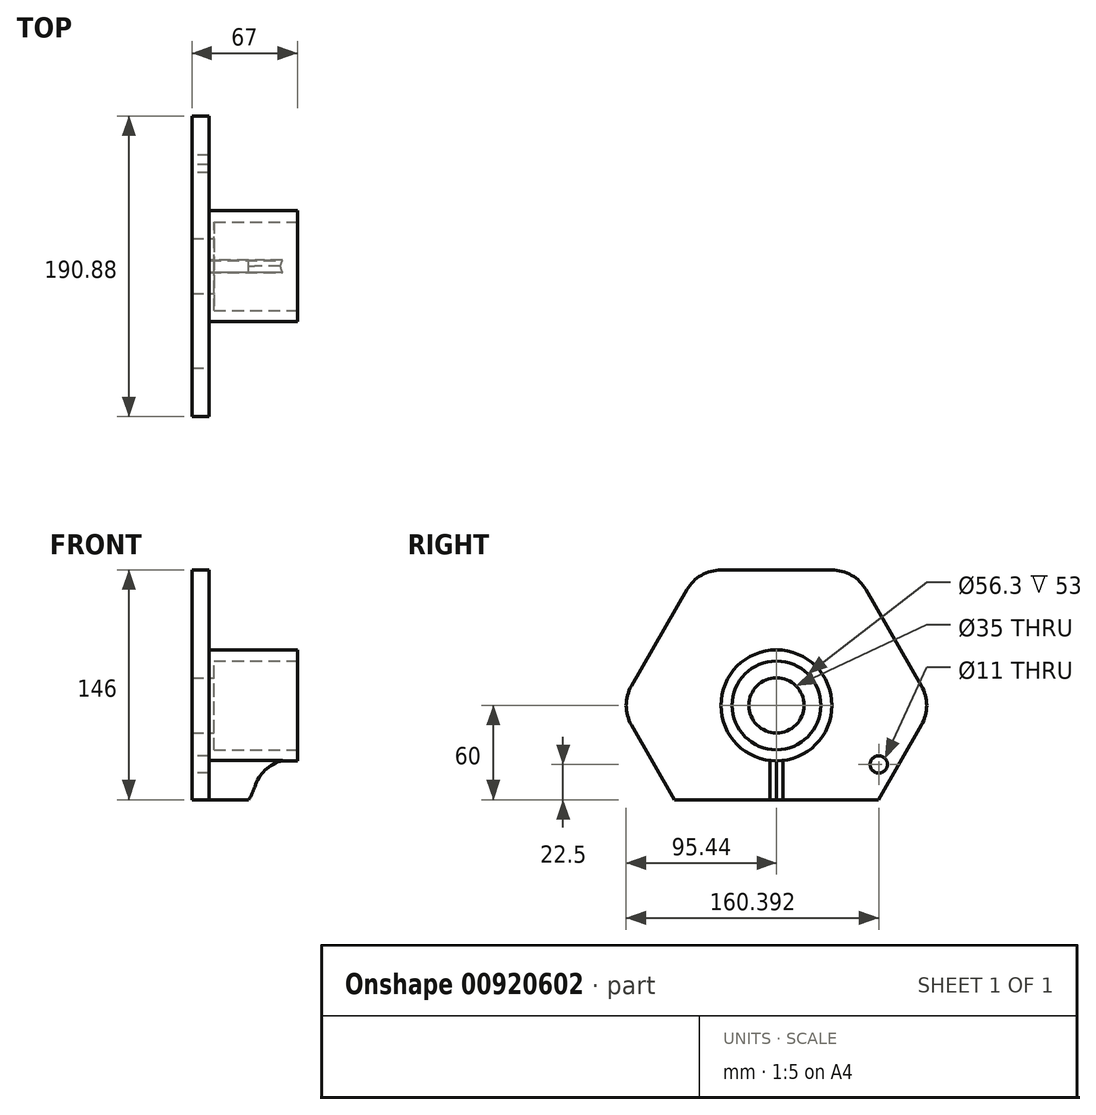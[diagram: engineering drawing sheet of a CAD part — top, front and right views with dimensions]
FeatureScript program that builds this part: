
annotation { "Feature Type Name" : "Feature", "Feature Type Description" : "" }
export const myFeature = defineFeature(function(context is Context, id is Id, definition is map)
    precondition{}
    {
        {
            var Q0;
            Q0=qCreatedBy(makeId("Front.planeOp"),FACE);
            var sketch = newSketch(context, id + "F0", { "sketchPlane" : qUnion([Q0])});
            skLineSegment(sketch, "E0.bottom", {"start": v(67, 35.25) * mm, "end": v(0, 35.25) * mm});
            skLineSegment(sketch, "E0.top", {"start": v(67, 28.15) * mm, "end": v(14, 28.15) * mm});
            skLineSegment(sketch, "E0.left", {"start": v(67, 35.25) * mm, "end": v(67, 28.15) * mm});
            skLineSegment(sketch, "E0.right", {"start": v(0, 35.25) * mm, "end": v(0, 0) * mm});
            skLineSegment(sketch, "E1", {"start": v(14, 0) * mm, "end": v(14, 28.15) * mm});
            skLineSegment(sketch, "E2", {"start": v(14, 0) * mm, "end": v(0, 0) * mm});
            skPoint(sketch, "E3.orphan", {"position": v(26.29, 0) * mm});
            skLineSegment(sketch, "E4", {"start": v(0, 0) * mm, "end": v(-45.98, 0) * mm, "construction": true});
            skSolve(sketch);
        }
        {
            var Q0;
            Q0=makeQuery(id+"F0.imprint","IMPRINT",FACE,{"disambiguationData":[TD([[makeQuery(id+"F0.imprint","IMPRINT",EDGE,{"derivedFrom":sQuery(id+"F0.wireOp",EDGE,"E0.bottom")}),1.0]])]});
            var Q1;
            Q1=sQuery(id+"F0.wireOp",EDGE,"E2");
            revolve(context, id + "F1", {"surfaceOperationType" : NewSurfaceOperationType.NEW, "entities" : qUnion([Q0]), "axis" : qUnion([Q1]), "revolveType" : RevolveType.FULL});
        }
        {
            var Q0;
            Q0=makeQuery(id+"F1.opRevolve","SWEPT_FACE",FACE,{"disambiguationData":[OSD([sQuery(id+"F0.wireOp",EDGE,"E0.right")])]});
            var sketch = newSketch(context, id + "F2", { "sketchPlane" : qUnion([Q0])});
            skCircle(sketch, "E5.cCircle", {"center": v(0, 0) * mm, "radius": 86 * mm, "construction": true});
            skLineSegment(sketch, "E5.0", {"start": v(-49.65, 86) * mm, "end": v(49.65, 86) * mm});
            skLineSegment(sketch, "E5.1", {"start": v(49.65, 86) * mm, "end": v(99.3, 0) * mm});
            skLineSegment(sketch, "E5.2", {"start": v(99.3, 0) * mm, "end": v(49.65, -86) * mm});
            skLineSegment(sketch, "E5.3", {"start": v(49.65, -86) * mm, "end": v(-49.65, -86) * mm});
            skLineSegment(sketch, "E5.4", {"start": v(-49.65, -86) * mm, "end": v(-99.3, 0) * mm});
            skLineSegment(sketch, "E5.5", {"start": v(-99.3, 0) * mm, "end": v(-49.65, 86) * mm});
            skPoint(sketch, "E5.0.midPoint", {"position": v(0, 86) * mm});
            skCircle(sketch, "E6", {"center": v(0, 0) * mm, "radius": 35.25 * mm});
            skSolve(sketch);
        }
        {
            var Q0;
            Q0=makeQuery(id+"F2.imprint","IMPRINT",FACE,{"disambiguationData":[TD([[makeQuery(id+"F2.imprint","IMPRINT",EDGE,{"derivedFrom":sQuery(id+"F2.wireOp",EDGE,"E5.0")}),-1.0]])]});
            extrude(context, id + "F3", {"entities" : qUnion([Q0]), "operationType" : NewBodyOperationType.ADD, "oppositeDirection" : true, "depth" : 11 * mm, "offsetDistance" : 25 * mm});
        }
        {
            var Q0;
            Q0=makeQuery(id+"F3.opExtrude","SWEPT_EDGE",EDGE,{"disambiguationData":[OSD([sQuery(id+"F2.wireOp",EDGE,"E5.3"),sQuery(id+"F2.wireOp",EDGE,"E5.4")])]});
            var Q1;
            Q1=makeQuery(id+"F3.opExtrude","SWEPT_EDGE",EDGE,{"disambiguationData":[OSD([sQuery(id+"F2.wireOp",EDGE,"E5.2"),sQuery(id+"F2.wireOp",EDGE,"E5.3")])]});
            var Q2;
            Q2=makeQuery(id+"F3.opExtrude","SWEPT_EDGE",EDGE,{"disambiguationData":[OSD([sQuery(id+"F2.wireOp",EDGE,"E5.1"),sQuery(id+"F2.wireOp",EDGE,"E5.2")])]});
            var Q3;
            Q3=makeQuery(id+"F3.opExtrude","SWEPT_EDGE",EDGE,{"disambiguationData":[OSD([sQuery(id+"F2.wireOp",EDGE,"E5.0"),sQuery(id+"F2.wireOp",EDGE,"E5.1")])]});
            var Q4;
            Q4=makeQuery(id+"F3.opExtrude","SWEPT_EDGE",EDGE,{"disambiguationData":[OSD([sQuery(id+"F2.wireOp",EDGE,"E5.4"),sQuery(id+"F2.wireOp",EDGE,"E5.5")])]});
            var Q5;
            Q5=makeQuery(id+"F3.opExtrude","SWEPT_EDGE",EDGE,{"disambiguationData":[OSD([sQuery(id+"F2.wireOp",EDGE,"E5.0"),sQuery(id+"F2.wireOp",EDGE,"E5.5")])]});
            fillet(context, id + "F4", {"entities" : qUnion([Q0, Q1, Q2, Q3, Q4, Q5]), "radius" : 25 * mm, "tangentPropagation" : true, "allowEdgeOverflow" : false});
        }
        {
            var Q0;
            Q0=qCreatedBy(makeId("Front.planeOp"),FACE);
            var sketch = newSketch(context, id + "F5", { "sketchPlane" : qUnion([Q0])});
            skLineSegment(sketch, "E7", {"start": v(67, -35.25) * mm, "end": v(11, -35.25) * mm, "construction": true});
            skLineSegment(sketch, "E8.0", {"start": v(11, -12.5) * mm, "end": v(11, -73.5) * mm, "construction": true});
            skLineSegment(sketch, "E9", {"start": v(56, -35.25) * mm, "end": v(11, -35.25) * mm});
            skLineSegment(sketch, "E10", {"start": v(11, -35.25) * mm, "end": v(11, -76) * mm});
            skArc(sketch, "E11", {"start": v(11, -76) * mm, "mid": v(28.9, -67.94) * mm, "end": v(39.73, -51.59) * mm});
            skArc(sketch, "E12", {"start": v(56, -35.25) * mm, "mid": v(45.87, -41.43) * mm, "end": v(39.73, -51.59) * mm});
            skSolve(sketch);
        }
        {
            var Q0;
            Q0=makeQuery(id+"F5.imprint","IMPRINT",FACE,{"disambiguationData":[TD([[makeQuery(id+"F5.imprint","IMPRINT",EDGE,{"derivedFrom":sQuery(id+"F5.wireOp",EDGE,"E9")}),1.0]])]});
            extrude(context, id + "F6", {"entities" : qUnion([Q0]), "operationType" : NewBodyOperationType.ADD, "depth" : 8 * mm, "offsetDistance" : 25 * mm, "hasDraft" : true, "draftAngle" : 3 * degree, "symmetric" : true});
        }
        {
            var Q0;
            Q0=makeQuery(id+"F3.boolean.opBoolean","MERGE",FACE,{"derivedFrom":[makeQuery(id+"F1.opRevolve","SWEPT_FACE",FACE,{"disambiguationData":[OSD([sQuery(id+"F0.wireOp",EDGE,"E0.right")])]}),makeQuery(id+"F3.opExtrude","CAP_FACE",FACE,{"disambiguationData":[OSD([sQuery(id+"F2.wireOp",EDGE,"E5.0"),sQuery(id+"F2.wireOp",EDGE,"E5.1"),sQuery(id+"F2.wireOp",EDGE,"E5.2"),sQuery(id+"F2.wireOp",EDGE,"E5.3"),sQuery(id+"F2.wireOp",EDGE,"E5.4"),sQuery(id+"F2.wireOp",EDGE,"E5.5"),sQuery(id+"F2.wireOp",EDGE,"E6")])],"isStart":true})]});
            var sketch = newSketch(context, id + "F7", { "sketchPlane" : qUnion([Q0])});
            skLineSegment(sketch, "E13.bottom", {"start": v(127.51, -130) * mm, "end": v(-152.25, -130) * mm});
            skLineSegment(sketch, "E13.top", {"start": v(127.51, -60) * mm, "end": v(-152.25, -60) * mm});
            skLineSegment(sketch, "E13.left", {"start": v(127.51, -130) * mm, "end": v(127.51, -60) * mm});
            skLineSegment(sketch, "E13.right", {"start": v(-152.25, -130) * mm, "end": v(-152.25, -60) * mm});
            skSolve(sketch);
        }
        {
            var Q0;
            {var subQ1=sQuery(id+"F2.wireOp",EDGE,"E5.3");Q0=makeQuery(id+"F7.imprint","IMPRINT",FACE,{"disambiguationData":[TD([[makeQuery(id+"F7.imprint","IMPRINT",EDGE,{"derivedFrom":makeQuery(id+"F3.opExtrude","CAP_EDGE",EDGE,{"disambiguationData":[OSD([subQ1])],"isStart":true})}),-1.0]])]});}
            var Q1;
            Q1=makeQuery(id+"F7.imprint","IMPRINT",FACE,{"disambiguationData":[TD([[makeQuery(id+"F7.imprint","IMPRINT",EDGE,{"derivedFrom":sQuery(id+"F7.wireOp",EDGE,"E13.bottom")}),-1.0]])]});
            extrude(context, id + "F8", {"entities" : qUnion([Q0, Q1]), "operationType" : NewBodyOperationType.REMOVE, "endBound" : BoundingType.THROUGH_ALL, "oppositeDirection" : true, "depth" : 25 * mm, "offsetDistance" : 25 * mm});
        }
        {
            var Q0;
            Q0=makeQuery(id+"F1.opRevolve","SWEPT_FACE",FACE,{"disambiguationData":[OSD([sQuery(id+"F0.wireOp",EDGE,"E1")])]});
            var sketch = newSketch(context, id + "F9", { "sketchPlane" : qUnion([Q0])});
            skCircle(sketch, "E14", {"center": v(0, 0) * mm, "radius": 17.5 * mm});
            skSolve(sketch);
        }
        {
            var Q0;
            Q0=makeQuery(id+"F9.imprint","IMPRINT",FACE,{"disambiguationData":[TD([[makeQuery(id+"F9.imprint","IMPRINT",EDGE,{"derivedFrom":sQuery(id+"F9.wireOp",EDGE,"E14")}),1.0]])]});
            extrude(context, id + "F10", {"entities" : qUnion([Q0]), "operationType" : NewBodyOperationType.REMOVE, "endBound" : BoundingType.THROUGH_ALL, "oppositeDirection" : true, "depth" : 25 * mm, "offsetDistance" : 25 * mm});
        }
        {
            var Q0;
            Q0=makeQuery(id+"F3.boolean.opBoolean","MERGE",FACE,{"derivedFrom":[makeQuery(id+"F1.opRevolve","SWEPT_FACE",FACE,{"disambiguationData":[OSD([sQuery(id+"F0.wireOp",EDGE,"E0.right")])]}),makeQuery(id+"F3.opExtrude","CAP_FACE",FACE,{"disambiguationData":[OSD([sQuery(id+"F2.wireOp",EDGE,"E5.0"),sQuery(id+"F2.wireOp",EDGE,"E5.1"),sQuery(id+"F2.wireOp",EDGE,"E5.2"),sQuery(id+"F2.wireOp",EDGE,"E5.3"),sQuery(id+"F2.wireOp",EDGE,"E5.4"),sQuery(id+"F2.wireOp",EDGE,"E5.5"),sQuery(id+"F2.wireOp",EDGE,"E6")])],"isStart":true})]});
            var sketch = newSketch(context, id + "F11", { "sketchPlane" : qUnion([Q0])});
            skLineSegment(sketch, "E15", {"start": v(0, 0) * mm, "end": v(-64.95, -37.5) * mm, "construction": true});
            skCircle(sketch, "E16", {"center": v(-64.95, -37.5) * mm, "radius": 5.5 * mm});
            skSolve(sketch);
        }
        {
            var Q0;
            Q0=makeQuery(id+"F11.imprint","IMPRINT",FACE,{"disambiguationData":[TD([[makeQuery(id+"F11.imprint","IMPRINT",EDGE,{"derivedFrom":sQuery(id+"F11.wireOp",EDGE,"E16")}),1.0]])]});
            extrude(context, id + "F12", {"entities" : qUnion([Q0]), "operationType" : NewBodyOperationType.REMOVE, "endBound" : BoundingType.THROUGH_ALL, "oppositeDirection" : true, "depth" : 25 * mm, "offsetDistance" : 25 * mm});
        }
    });
